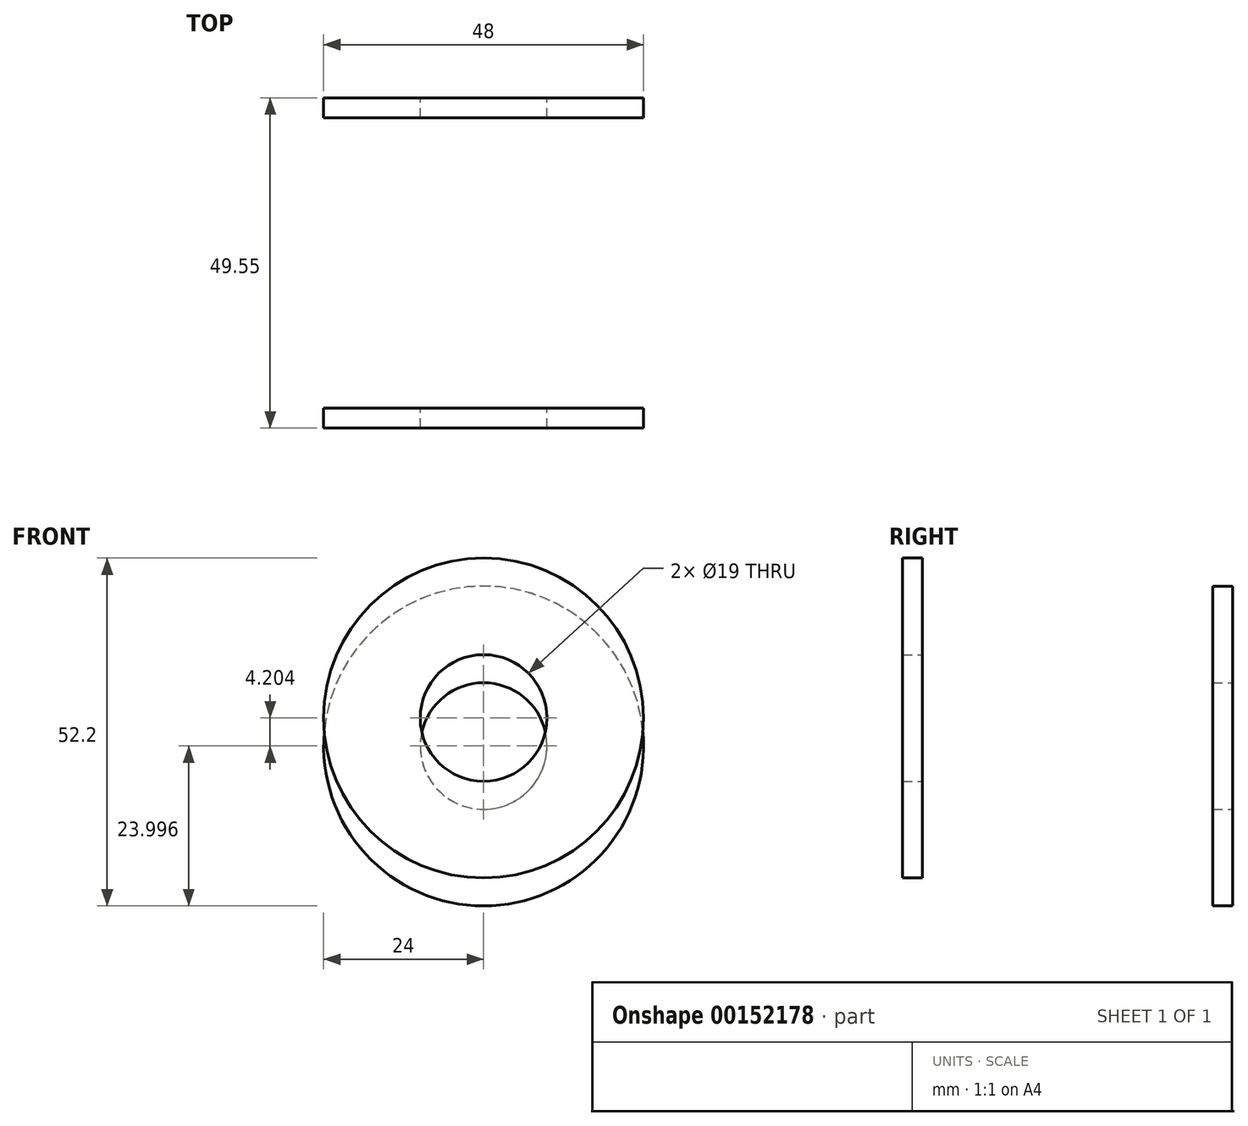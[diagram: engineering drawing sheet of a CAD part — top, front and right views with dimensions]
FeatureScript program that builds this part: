
annotation { "Feature Type Name" : "Feature", "Feature Type Description" : "" }
export const myFeature = defineFeature(function(context is Context, id is Id, definition is map)
    precondition{}
    {
        {
            var Q0;
            Q0=qCreatedBy(makeId("Front.planeOp"),FACE);
            var sketch = newSketch(context, id + "F0", { "sketchPlane" : qUnion([Q0])});
            skCircle(sketch, "E0", {"center": v(0, 0) * mm, "radius": 24 * mm});
            skCircle(sketch, "E1", {"center": v(0, 0) * mm, "radius": 9.5 * mm});
            skSolve(sketch);
        }
        {
            var Q0;
            Q0=qSketchRegion(id+"F0",true);
            extrude(context, id + "F1", {"entities" : qUnion([Q0]), "depth" : 3 * mm});
        }
        {
            var Q0;
            Q0=makeQuery(id+"F1.opExtrude","SWEPT_BODY",BODY,{"disambiguationData":[OSD([sQuery(id+"F0.wireOp",EDGE,"E0"),sQuery(id+"F0.wireOp",EDGE,"E1")])]});
            transform(context, id + "F2", {"entities" : qUnion([Q0]), "transformType" : TransformType.TRANSLATION_3D, "dx" : 0 * mm, "dy" : 0 * mm, "dz" : 0 * mm, "makeCopy" : true});
        }
        {
            var Q0;
            Q0=makeQuery(id+"F2.opPattern","COPY",BODY,{"derivedFrom":makeQuery(id+"F1.opExtrude","SWEPT_BODY",BODY,{"disambiguationData":[OSD([sQuery(id+"F0.wireOp",EDGE,"E0"),sQuery(id+"F0.wireOp",EDGE,"E1")])]}),"instanceName":"1"});
            deleteBodies(context, id + "F3", {"entities" : qUnion([Q0])});
        }
        {
            var Q0;
            Q0=makeQuery(id+"F1.opExtrude","SWEPT_BODY",BODY,{"disambiguationData":[OSD([sQuery(id+"F0.wireOp",EDGE,"E0"),sQuery(id+"F0.wireOp",EDGE,"E1")])]});
            transform(context, id + "F4", {"entities" : qUnion([Q0]), "transformType" : TransformType.TRANSLATION_3D, "dx" : 0 * mm, "dy" : 46.55 * mm, "dz" : -4.2 * mm, "makeCopy" : true});
        }
    });
